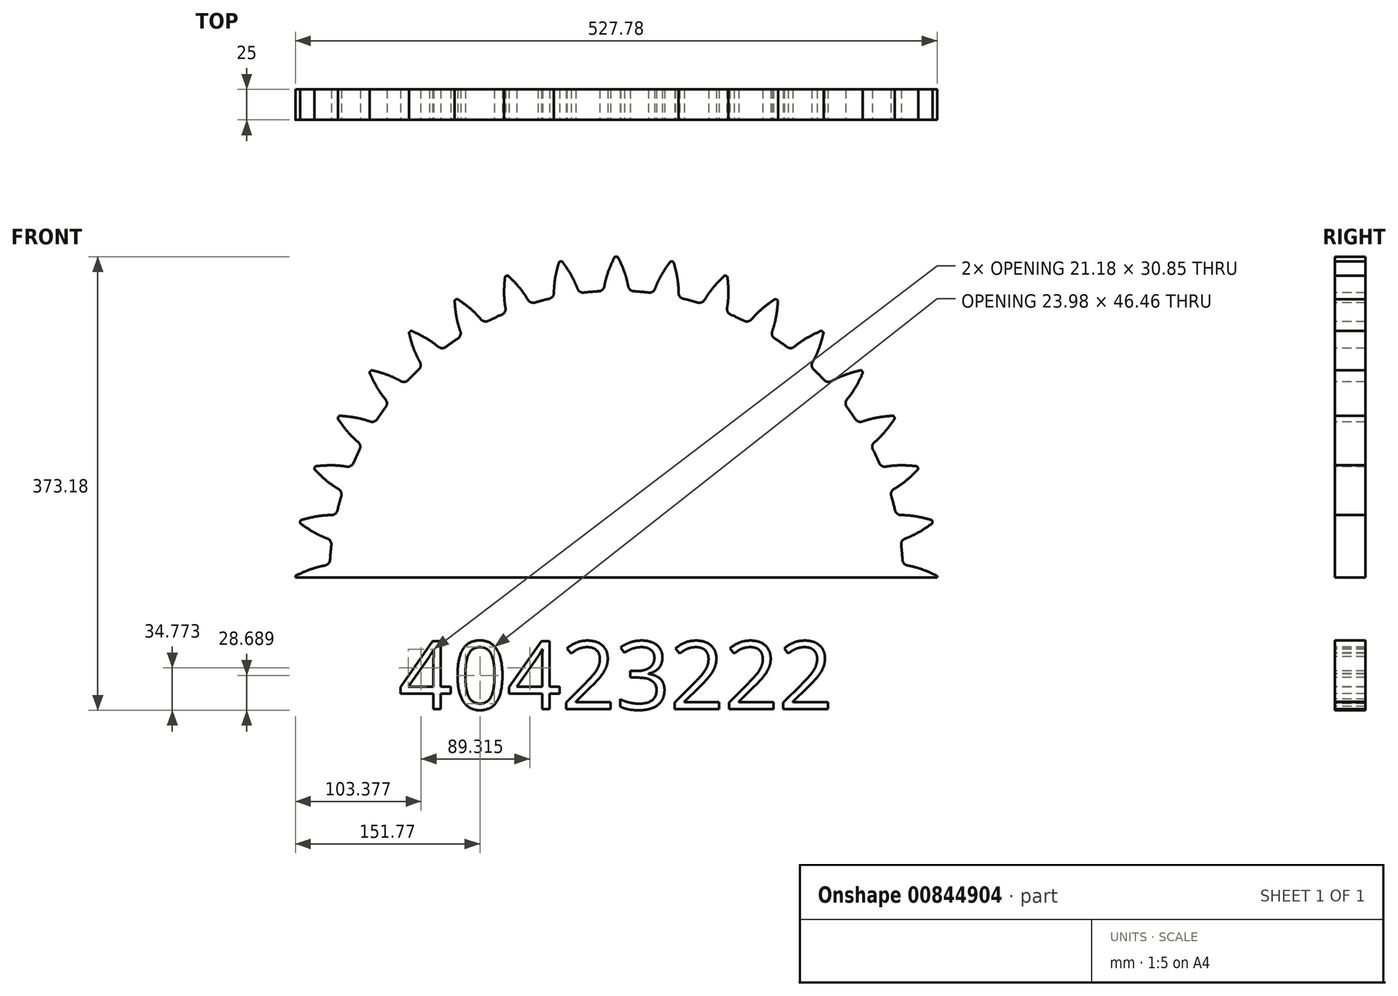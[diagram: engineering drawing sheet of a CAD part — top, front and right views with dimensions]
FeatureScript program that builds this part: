
annotation { "Feature Type Name" : "Feature", "Feature Type Description" : "" }
export const myFeature = defineFeature(function(context is Context, id is Id, definition is map)
    precondition{}
    {
        {
            var Q0;
            Q0=qCreatedBy(makeId("Front.planeOp"),FACE);
            var sketch = newSketch(context, id + "F0", { "sketchPlane" : qUnion([Q0])});
            skLineSegment(sketch, "E0.bottom", {"start": v(400, 300) * mm, "end": v(-400, 300) * mm});
            skLineSegment(sketch, "E0.top", {"start": v(400, -300) * mm, "end": v(-400, -300) * mm});
            skLineSegment(sketch, "E0.left", {"start": v(400, 300) * mm, "end": v(400, -300) * mm});
            skLineSegment(sketch, "E0.right", {"start": v(-400, 300) * mm, "end": v(-400, -300) * mm});
            skPoint(sketch, "E0.middle", {"position": v(0, 0) * mm});
            skCircle(sketch, "E1", {"center": v(0, 0) * mm, "radius": 250 * mm});
            skText(sketch, "E2", { "text": "Module = 500/36 = 13.888", "fontName": "OpenSans-Regular.ttf"});
            skCircle(sketch, "E3.0", {"center": v(0, 0) * mm, "radius": 263.89 * mm});
            skCircle(sketch, "E4.0", {"center": v(0, 0) * mm, "radius": 235.81 * mm});
            skPoint(sketch, "E5", {"position": v(29.73, 248.23) * mm});
            skArc(sketch, "E6", {"start": v(-38.46, 231.75) * mm, "mid": v(0.39, -234.92) * mm, "end": v(37.69, 231.88) * mm});
            skLineSegment(sketch, "E7", {"start": v(106.03, 209.63) * mm, "end": v(0, 0) * mm});
            skLineSegment(sketch, "E8", {"start": v(84.05, 219.37) * mm, "end": v(0, 0) * mm});
            skLineSegment(sketch, "E9", {"start": v(61.2, 226.81) * mm, "end": v(0, 0) * mm});
            skLineSegment(sketch, "E10", {"start": v(37.69, 231.88) * mm, "end": v(0, 0) * mm});
            skFitSpline(sketch, "E11", {"points": [v(-10.25, 234.7) * mm, v(-10.2, 235.93) * mm, v(-9.77, 239.6) * mm, v(-8.44, 245.6) * mm, v(-5.74, 253.78) * mm, v(-1.23, 263.89) * mm], "startDerivative": vector(-1.24, 11.37) * mm, "endDerivative": vector(17.19, 36.05) * mm});
            skLineSegment(sketch, "E12", {"start": v(0, -334.79) * mm, "end": v(0, 396.98) * mm, "construction": true});
            skFitSpline(sketch, "E13.MirrorCS", {"points": [v(10.25, 234.7) * mm, v(10.2, 235.93) * mm, v(9.77, 239.6) * mm, v(8.44, 245.6) * mm, v(5.74, 253.78) * mm, v(1.23, 263.89) * mm], "startDerivative": vector(1.24, 11.37) * mm, "endDerivative": vector(-17.19, 36.05) * mm});
            skLineSegment(sketch, "E14", {"start": v(-10.24, 235.59) * mm, "end": v(0, 0) * mm});
            skLineSegment(sketch, "E15", {"start": v(10.24, 235.59) * mm, "end": v(0, 0) * mm});
            skLineSegment(sketch, "E16", {"start": v(0, 0) * mm, "end": v(-38.6, 232.63) * mm});
            skLineSegment(sketch, "E17", {"start": v(37.69, 231.88) * mm, "end": v(37.83, 232.76) * mm});
            const initialGuessF0  = {"E2": [-0.85754, 0.4595, 1, 0, 0.10541]};
            skSetInitialGuess(sketch, initialGuessF0);
            skSolve(sketch);
        }
        {
            var Q0;
            {var subQ0=sQuery(id+"F0.wireOp",EDGE,"E11");var subQ1=sQuery(id+"F0.wireOp",EDGE,"E1");var subQ2=makeQuery(id+"F0.imprint","INTERSECT",VERTEX,{"derivedFrom":[subQ1,subQ0]});Q0=makeQuery(id+"F0.imprint","IMPRINT",FACE,{"disambiguationData":[TD([[makeQuery(id+"F0.imprint","IMPRINT",EDGE,{"disambiguationData":[TD([[subQ2,1.0]])],"derivedFrom":subQ1}),1.0]])]});}
            var Q1;
            {var subQ0=sQuery(id+"F0.wireOp",EDGE,"E11");var subQ1=sQuery(id+"F0.wireOp",EDGE,"E1");var subQ2=makeQuery(id+"F0.imprint","INTERSECT",VERTEX,{"derivedFrom":[subQ1,subQ0]});Q1=makeQuery(id+"F0.imprint","IMPRINT",FACE,{"disambiguationData":[TD([[makeQuery(id+"F0.imprint","IMPRINT",EDGE,{"disambiguationData":[TD([[subQ2,1.0]])],"derivedFrom":subQ1}),-1.0]])]});}
            var Q2;
            {var subQ0=sQuery(id+"F0.wireOp",EDGE,"E14");Q2=makeQuery(id+"F0.imprint","IMPRINT",FACE,{"disambiguationData":[TD([[makeQuery(id+"F0.imprint","IMPRINT",EDGE,{"derivedFrom":subQ0}),1.0]])]});}
            var Q3;
            {var subQ0=sQuery(id+"F0.wireOp",EDGE,"E14");Q3=makeQuery(id+"F0.imprint","IMPRINT",FACE,{"disambiguationData":[TD([[makeQuery(id+"F0.imprint","IMPRINT",EDGE,{"derivedFrom":subQ0}),-1.0]])]});}
            var Q4;
            Q4=makeQuery(id+"F0.imprint","IMPRINT",FACE,{"disambiguationData":[TD([[makeQuery(id+"F0.imprint","IMPRINT",EDGE,{"derivedFrom":sQuery(id+"F0.wireOp",EDGE,"E10")}),-1.0]])]});
            extrude(context, id + "F1", {"entities" : qUnion([Q0, Q1, Q2, Q3, Q4]), "oppositeDirection" : true, "depth" : 25 * mm, "offsetDistance" : 25 * mm});
        }
        {
            var Q0;
            Q0=makeQuery(id+"F1.opExtrude","SWEPT_EDGE",EDGE,{"disambiguationData":[OSD([sQuery(id+"F0.wireOp",EDGE,"E3.0"),sQuery(id+"F0.wireOp",EDGE,"E13.MirrorCS")])]});
            var Q1;
            Q1=makeQuery(id+"F1.opExtrude","SWEPT_EDGE",EDGE,{"disambiguationData":[OSD([sQuery(id+"F0.wireOp",EDGE,"E3.0"),sQuery(id+"F0.wireOp",EDGE,"E11")])]});
            fillet(context, id + "F2", {"entities" : qUnion([Q0, Q1]), "radius" : 1 * mm, "tangentPropagation" : true, "allowEdgeOverflow" : false});
        }
        {
            var Q0;
            Q0=makeQuery(id+"F1.opExtrude","SWEPT_EDGE",EDGE,{"disambiguationData":[OSD([sQuery(id+"F0.wireOp",EDGE,"E4.0"),sQuery(id+"F0.wireOp",EDGE,"E13.MirrorCS"),sQuery(id+"F0.wireOp",EDGE,"E15")])]});
            var Q1;
            Q1=makeQuery(id+"F1.opExtrude","SWEPT_EDGE",EDGE,{"disambiguationData":[OSD([sQuery(id+"F0.wireOp",EDGE,"E4.0"),sQuery(id+"F0.wireOp",EDGE,"E11"),sQuery(id+"F0.wireOp",EDGE,"E14")])]});
            fillet(context, id + "F3", {"entities" : qUnion([Q0, Q1]), "radius" : 5 * mm, "tangentPropagation" : true, "allowEdgeOverflow" : false});
        }
        {
            var Q0;
            Q0=qCreatedBy(makeId("Top.planeOp"),FACE);
            var sketch = newSketch(context, id + "F4", { "sketchPlane" : qUnion([Q0])});
            skLineSegment(sketch, "E18", {"start": v(0, 43.7) * mm, "end": v(0, -32.4) * mm, "construction": true});
            skSolve(sketch);
        }
        {
            var Q0;
            Q0=makeQuery(id+"F1.opExtrude","SWEPT_BODY",BODY,{"disambiguationData":[OSD([sQuery(id+"F0.wireOp",EDGE,"E3.0"),sQuery(id+"F0.wireOp",EDGE,"E4.0"),sQuery(id+"F0.wireOp",EDGE,"E10"),sQuery(id+"F0.wireOp",EDGE,"E11"),sQuery(id+"F0.wireOp",EDGE,"E13.MirrorCS"),sQuery(id+"F0.wireOp",EDGE,"E16"),sQuery(id+"F0.wireOp",EDGE,"E17")])]});
            var Q1;
            Q1=sQuery(id+"F4.wireOp",EDGE,"E18");
            circularPattern(context, id + "F5", {"operationType" : NewBodyOperationType.ADD, "entities" : qUnion([Q0]), "axis" : qUnion([Q1]), "angle" : 360 * degree, "instanceCount" : 36, "equalSpace" : true});
        }
        {
            var Q0;
            {var subQ1=sQuery(id+"F0.wireOp",EDGE,"E13.MirrorCS");var subQ2=sQuery(id+"F0.wireOp",EDGE,"E4.0");var subQ7=sQuery(id+"F0.wireOp",EDGE,"E11");var subQ8=sQuery(id+"F0.wireOp",EDGE,"E16");var subQ11=sQuery(id+"F0.wireOp",EDGE,"E3.0");var subQ17=makeQuery(id+"F1.opExtrude","SWEPT_FACE",FACE,{"disambiguationData":[OSD([subQ11])]});var subQ19=sQuery(id+"F0.wireOp",EDGE,"E17");var subQ20=makeQuery(id+"F1.opExtrude","CAP_FACE",FACE,{"disambiguationData":[OSD([subQ11,subQ2,sQuery(id+"F0.wireOp",EDGE,"E10"),subQ7,subQ1,subQ8,subQ19])],"isStart":true});Q0=makeQuery(id+"F9.boolean.opBoolean","SPLIT",FACE,{"disambiguationData":[TD([subQ17])],"derivedFrom":makeQuery(id+"F5.boolean.opBoolean","MERGE",FACE,{"derivedFrom":[subQ20,makeQuery(id+"F5.opPattern","COPY",FACE,{"derivedFrom":subQ20,"instanceName":"1"}),makeQuery(id+"F5.opPattern","COPY",FACE,{"derivedFrom":subQ20,"instanceName":"2"}),makeQuery(id+"F5.opPattern","COPY",FACE,{"derivedFrom":subQ20,"instanceName":"3"}),makeQuery(id+"F5.opPattern","COPY",FACE,{"derivedFrom":subQ20,"instanceName":"4"}),makeQuery(id+"F5.opPattern","COPY",FACE,{"derivedFrom":subQ20,"instanceName":"5"}),makeQuery(id+"F5.opPattern","COPY",FACE,{"derivedFrom":subQ20,"instanceName":"6"}),makeQuery(id+"F5.opPattern","COPY",FACE,{"derivedFrom":subQ20,"instanceName":"7"}),makeQuery(id+"F5.opPattern","COPY",FACE,{"derivedFrom":subQ20,"instanceName":"8"}),makeQuery(id+"F5.opPattern","COPY",FACE,{"derivedFrom":subQ20,"instanceName":"9"}),makeQuery(id+"F5.opPattern","COPY",FACE,{"derivedFrom":subQ20,"instanceName":"10"}),makeQuery(id+"F5.opPattern","COPY",FACE,{"derivedFrom":subQ20,"instanceName":"11"}),makeQuery(id+"F5.opPattern","COPY",FACE,{"derivedFrom":subQ20,"instanceName":"12"}),makeQuery(id+"F5.opPattern","COPY",FACE,{"derivedFrom":subQ20,"instanceName":"13"}),makeQuery(id+"F5.opPattern","COPY",FACE,{"derivedFrom":subQ20,"instanceName":"14"}),makeQuery(id+"F5.opPattern","COPY",FACE,{"derivedFrom":subQ20,"instanceName":"15"}),makeQuery(id+"F5.opPattern","COPY",FACE,{"derivedFrom":subQ20,"instanceName":"16"}),makeQuery(id+"F5.opPattern","COPY",FACE,{"derivedFrom":subQ20,"instanceName":"17"}),makeQuery(id+"F5.opPattern","COPY",FACE,{"derivedFrom":subQ20,"instanceName":"18"}),makeQuery(id+"F5.opPattern","COPY",FACE,{"derivedFrom":subQ20,"instanceName":"19"}),makeQuery(id+"F5.opPattern","COPY",FACE,{"derivedFrom":subQ20,"instanceName":"20"}),makeQuery(id+"F5.opPattern","COPY",FACE,{"derivedFrom":subQ20,"instanceName":"21"}),makeQuery(id+"F5.opPattern","COPY",FACE,{"derivedFrom":subQ20,"instanceName":"22"}),makeQuery(id+"F5.opPattern","COPY",FACE,{"derivedFrom":subQ20,"instanceName":"23"}),makeQuery(id+"F5.opPattern","COPY",FACE,{"derivedFrom":subQ20,"instanceName":"24"}),makeQuery(id+"F5.opPattern","COPY",FACE,{"derivedFrom":subQ20,"instanceName":"25"}),makeQuery(id+"F5.opPattern","COPY",FACE,{"derivedFrom":subQ20,"instanceName":"26"}),makeQuery(id+"F5.opPattern","COPY",FACE,{"derivedFrom":subQ20,"instanceName":"27"}),makeQuery(id+"F5.opPattern","COPY",FACE,{"derivedFrom":subQ20,"instanceName":"28"}),makeQuery(id+"F5.opPattern","COPY",FACE,{"derivedFrom":subQ20,"instanceName":"29"}),makeQuery(id+"F5.opPattern","COPY",FACE,{"derivedFrom":subQ20,"instanceName":"30"}),makeQuery(id+"F5.opPattern","COPY",FACE,{"derivedFrom":subQ20,"instanceName":"31"}),makeQuery(id+"F5.opPattern","COPY",FACE,{"derivedFrom":subQ20,"instanceName":"32"}),makeQuery(id+"F5.opPattern","COPY",FACE,{"derivedFrom":subQ20,"instanceName":"33"}),makeQuery(id+"F5.opPattern","COPY",FACE,{"derivedFrom":subQ20,"instanceName":"34"}),makeQuery(id+"F5.opPattern","COPY",FACE,{"derivedFrom":subQ20,"instanceName":"35"})]})});}
            var sketch = newSketch(context, id + "F6", { "sketchPlane" : qUnion([Q0])});
            skLineSegment(sketch, "E19.bottom", {"start": v(-283.2, 0) * mm, "end": v(319.71, 0) * mm});
            skLineSegment(sketch, "E19.top", {"start": v(-283.2, -271.72) * mm, "end": v(319.71, -271.72) * mm});
            skLineSegment(sketch, "E19.left", {"start": v(-283.2, 0) * mm, "end": v(-283.2, -271.72) * mm});
            skLineSegment(sketch, "E19.right", {"start": v(319.71, 0) * mm, "end": v(319.71, -271.72) * mm});
            skSolve(sketch);
        }
        {
            var Q0;
            Q0 = qSketchRegion(id + "F6", true);
            var Q1;
            {var subQ0=makeQuery(id+"F1.opExtrude","CAP_FACE",FACE,{"disambiguationData":[OSD([sQuery(id+"F0.wireOp",EDGE,"E3.0"),sQuery(id+"F0.wireOp",EDGE,"E4.0"),sQuery(id+"F0.wireOp",EDGE,"E10"),sQuery(id+"F0.wireOp",EDGE,"E11"),sQuery(id+"F0.wireOp",EDGE,"E13.MirrorCS"),sQuery(id+"F0.wireOp",EDGE,"E16"),sQuery(id+"F0.wireOp",EDGE,"E17")])],"isStart":false});Q1=makeQuery(id+"F5.boolean.opBoolean","MERGE",FACE,{"derivedFrom":[subQ0,makeQuery(id+"F5.opPattern","COPY",FACE,{"derivedFrom":subQ0,"instanceName":"1"}),makeQuery(id+"F5.opPattern","COPY",FACE,{"derivedFrom":subQ0,"instanceName":"2"}),makeQuery(id+"F5.opPattern","COPY",FACE,{"derivedFrom":subQ0,"instanceName":"3"}),makeQuery(id+"F5.opPattern","COPY",FACE,{"derivedFrom":subQ0,"instanceName":"4"}),makeQuery(id+"F5.opPattern","COPY",FACE,{"derivedFrom":subQ0,"instanceName":"5"}),makeQuery(id+"F5.opPattern","COPY",FACE,{"derivedFrom":subQ0,"instanceName":"6"}),makeQuery(id+"F5.opPattern","COPY",FACE,{"derivedFrom":subQ0,"instanceName":"7"}),makeQuery(id+"F5.opPattern","COPY",FACE,{"derivedFrom":subQ0,"instanceName":"8"}),makeQuery(id+"F5.opPattern","COPY",FACE,{"derivedFrom":subQ0,"instanceName":"9"}),makeQuery(id+"F5.opPattern","COPY",FACE,{"derivedFrom":subQ0,"instanceName":"10"}),makeQuery(id+"F5.opPattern","COPY",FACE,{"derivedFrom":subQ0,"instanceName":"11"}),makeQuery(id+"F5.opPattern","COPY",FACE,{"derivedFrom":subQ0,"instanceName":"12"}),makeQuery(id+"F5.opPattern","COPY",FACE,{"derivedFrom":subQ0,"instanceName":"13"}),makeQuery(id+"F5.opPattern","COPY",FACE,{"derivedFrom":subQ0,"instanceName":"14"}),makeQuery(id+"F5.opPattern","COPY",FACE,{"derivedFrom":subQ0,"instanceName":"15"}),makeQuery(id+"F5.opPattern","COPY",FACE,{"derivedFrom":subQ0,"instanceName":"16"}),makeQuery(id+"F5.opPattern","COPY",FACE,{"derivedFrom":subQ0,"instanceName":"17"}),makeQuery(id+"F5.opPattern","COPY",FACE,{"derivedFrom":subQ0,"instanceName":"18"}),makeQuery(id+"F5.opPattern","COPY",FACE,{"derivedFrom":subQ0,"instanceName":"19"}),makeQuery(id+"F5.opPattern","COPY",FACE,{"derivedFrom":subQ0,"instanceName":"20"}),makeQuery(id+"F5.opPattern","COPY",FACE,{"derivedFrom":subQ0,"instanceName":"21"}),makeQuery(id+"F5.opPattern","COPY",FACE,{"derivedFrom":subQ0,"instanceName":"22"}),makeQuery(id+"F5.opPattern","COPY",FACE,{"derivedFrom":subQ0,"instanceName":"23"}),makeQuery(id+"F5.opPattern","COPY",FACE,{"derivedFrom":subQ0,"instanceName":"24"}),makeQuery(id+"F5.opPattern","COPY",FACE,{"derivedFrom":subQ0,"instanceName":"25"}),makeQuery(id+"F5.opPattern","COPY",FACE,{"derivedFrom":subQ0,"instanceName":"26"}),makeQuery(id+"F5.opPattern","COPY",FACE,{"derivedFrom":subQ0,"instanceName":"27"}),makeQuery(id+"F5.opPattern","COPY",FACE,{"derivedFrom":subQ0,"instanceName":"28"}),makeQuery(id+"F5.opPattern","COPY",FACE,{"derivedFrom":subQ0,"instanceName":"29"}),makeQuery(id+"F5.opPattern","COPY",FACE,{"derivedFrom":subQ0,"instanceName":"30"}),makeQuery(id+"F5.opPattern","COPY",FACE,{"derivedFrom":subQ0,"instanceName":"31"}),makeQuery(id+"F5.opPattern","COPY",FACE,{"derivedFrom":subQ0,"instanceName":"32"}),makeQuery(id+"F5.opPattern","COPY",FACE,{"derivedFrom":subQ0,"instanceName":"33"}),makeQuery(id+"F5.opPattern","COPY",FACE,{"derivedFrom":subQ0,"instanceName":"34"}),makeQuery(id+"F5.opPattern","COPY",FACE,{"derivedFrom":subQ0,"instanceName":"35"})]});}
            extrude(context, id + "F7", {"entities" : qUnion([Q0]), "operationType" : NewBodyOperationType.REMOVE, "endBound" : BoundingType.UP_TO_SURFACE, "oppositeDirection" : true, "depth" : 25 * mm, "endBoundEntityFace" : qUnion([Q1]), "offsetDistance" : 25 * mm});
        }
        {
            var Q0;
            {var subQ0=makeQuery(id+"F1.opExtrude","CAP_FACE",FACE,{"disambiguationData":[OSD([sQuery(id+"F0.wireOp",EDGE,"E3.0"),sQuery(id+"F0.wireOp",EDGE,"E4.0"),sQuery(id+"F0.wireOp",EDGE,"E10"),sQuery(id+"F0.wireOp",EDGE,"E11"),sQuery(id+"F0.wireOp",EDGE,"E13.MirrorCS"),sQuery(id+"F0.wireOp",EDGE,"E16"),sQuery(id+"F0.wireOp",EDGE,"E17")])],"isStart":true});Q0=makeQuery(id+"F5.boolean.opBoolean","MERGE",FACE,{"derivedFrom":[subQ0,makeQuery(id+"F5.opPattern","COPY",FACE,{"derivedFrom":subQ0,"instanceName":"1"}),makeQuery(id+"F5.opPattern","COPY",FACE,{"derivedFrom":subQ0,"instanceName":"2"}),makeQuery(id+"F5.opPattern","COPY",FACE,{"derivedFrom":subQ0,"instanceName":"3"}),makeQuery(id+"F5.opPattern","COPY",FACE,{"derivedFrom":subQ0,"instanceName":"4"}),makeQuery(id+"F5.opPattern","COPY",FACE,{"derivedFrom":subQ0,"instanceName":"5"}),makeQuery(id+"F5.opPattern","COPY",FACE,{"derivedFrom":subQ0,"instanceName":"6"}),makeQuery(id+"F5.opPattern","COPY",FACE,{"derivedFrom":subQ0,"instanceName":"7"}),makeQuery(id+"F5.opPattern","COPY",FACE,{"derivedFrom":subQ0,"instanceName":"8"}),makeQuery(id+"F5.opPattern","COPY",FACE,{"derivedFrom":subQ0,"instanceName":"9"}),makeQuery(id+"F5.opPattern","COPY",FACE,{"derivedFrom":subQ0,"instanceName":"10"}),makeQuery(id+"F5.opPattern","COPY",FACE,{"derivedFrom":subQ0,"instanceName":"11"}),makeQuery(id+"F5.opPattern","COPY",FACE,{"derivedFrom":subQ0,"instanceName":"12"}),makeQuery(id+"F5.opPattern","COPY",FACE,{"derivedFrom":subQ0,"instanceName":"13"}),makeQuery(id+"F5.opPattern","COPY",FACE,{"derivedFrom":subQ0,"instanceName":"14"}),makeQuery(id+"F5.opPattern","COPY",FACE,{"derivedFrom":subQ0,"instanceName":"15"}),makeQuery(id+"F5.opPattern","COPY",FACE,{"derivedFrom":subQ0,"instanceName":"16"}),makeQuery(id+"F5.opPattern","COPY",FACE,{"derivedFrom":subQ0,"instanceName":"17"}),makeQuery(id+"F5.opPattern","COPY",FACE,{"derivedFrom":subQ0,"instanceName":"18"}),makeQuery(id+"F5.opPattern","COPY",FACE,{"derivedFrom":subQ0,"instanceName":"19"}),makeQuery(id+"F5.opPattern","COPY",FACE,{"derivedFrom":subQ0,"instanceName":"20"}),makeQuery(id+"F5.opPattern","COPY",FACE,{"derivedFrom":subQ0,"instanceName":"21"}),makeQuery(id+"F5.opPattern","COPY",FACE,{"derivedFrom":subQ0,"instanceName":"22"}),makeQuery(id+"F5.opPattern","COPY",FACE,{"derivedFrom":subQ0,"instanceName":"23"}),makeQuery(id+"F5.opPattern","COPY",FACE,{"derivedFrom":subQ0,"instanceName":"24"}),makeQuery(id+"F5.opPattern","COPY",FACE,{"derivedFrom":subQ0,"instanceName":"25"}),makeQuery(id+"F5.opPattern","COPY",FACE,{"derivedFrom":subQ0,"instanceName":"26"}),makeQuery(id+"F5.opPattern","COPY",FACE,{"derivedFrom":subQ0,"instanceName":"27"}),makeQuery(id+"F5.opPattern","COPY",FACE,{"derivedFrom":subQ0,"instanceName":"28"}),makeQuery(id+"F5.opPattern","COPY",FACE,{"derivedFrom":subQ0,"instanceName":"29"}),makeQuery(id+"F5.opPattern","COPY",FACE,{"derivedFrom":subQ0,"instanceName":"30"}),makeQuery(id+"F5.opPattern","COPY",FACE,{"derivedFrom":subQ0,"instanceName":"31"}),makeQuery(id+"F5.opPattern","COPY",FACE,{"derivedFrom":subQ0,"instanceName":"32"}),makeQuery(id+"F5.opPattern","COPY",FACE,{"derivedFrom":subQ0,"instanceName":"33"}),makeQuery(id+"F5.opPattern","COPY",FACE,{"derivedFrom":subQ0,"instanceName":"34"}),makeQuery(id+"F5.opPattern","COPY",FACE,{"derivedFrom":subQ0,"instanceName":"35"})]});}
            var sketch = newSketch(context, id + "F8", { "sketchPlane" : qUnion([Q0])});
            skText(sketch, "E20", { "text": "40423222", "fontName": "OpenSans-Regular.ttf"});
            const initialGuessF8  = {"E20": [-0.17907, -0.10852, 1, 0, 0.05624]};
            skSetInitialGuess(sketch, initialGuessF8);
            skSolve(sketch);
        }
        {
            var Q0;
            Q0=qSketchRegion(id+"F8",true);
            extrude(context, id + "F9", {"entities" : qUnion([Q0]), "oppositeDirection" : true, "depth" : 25 * mm, "offsetDistance" : 25 * mm});
        }
    });
